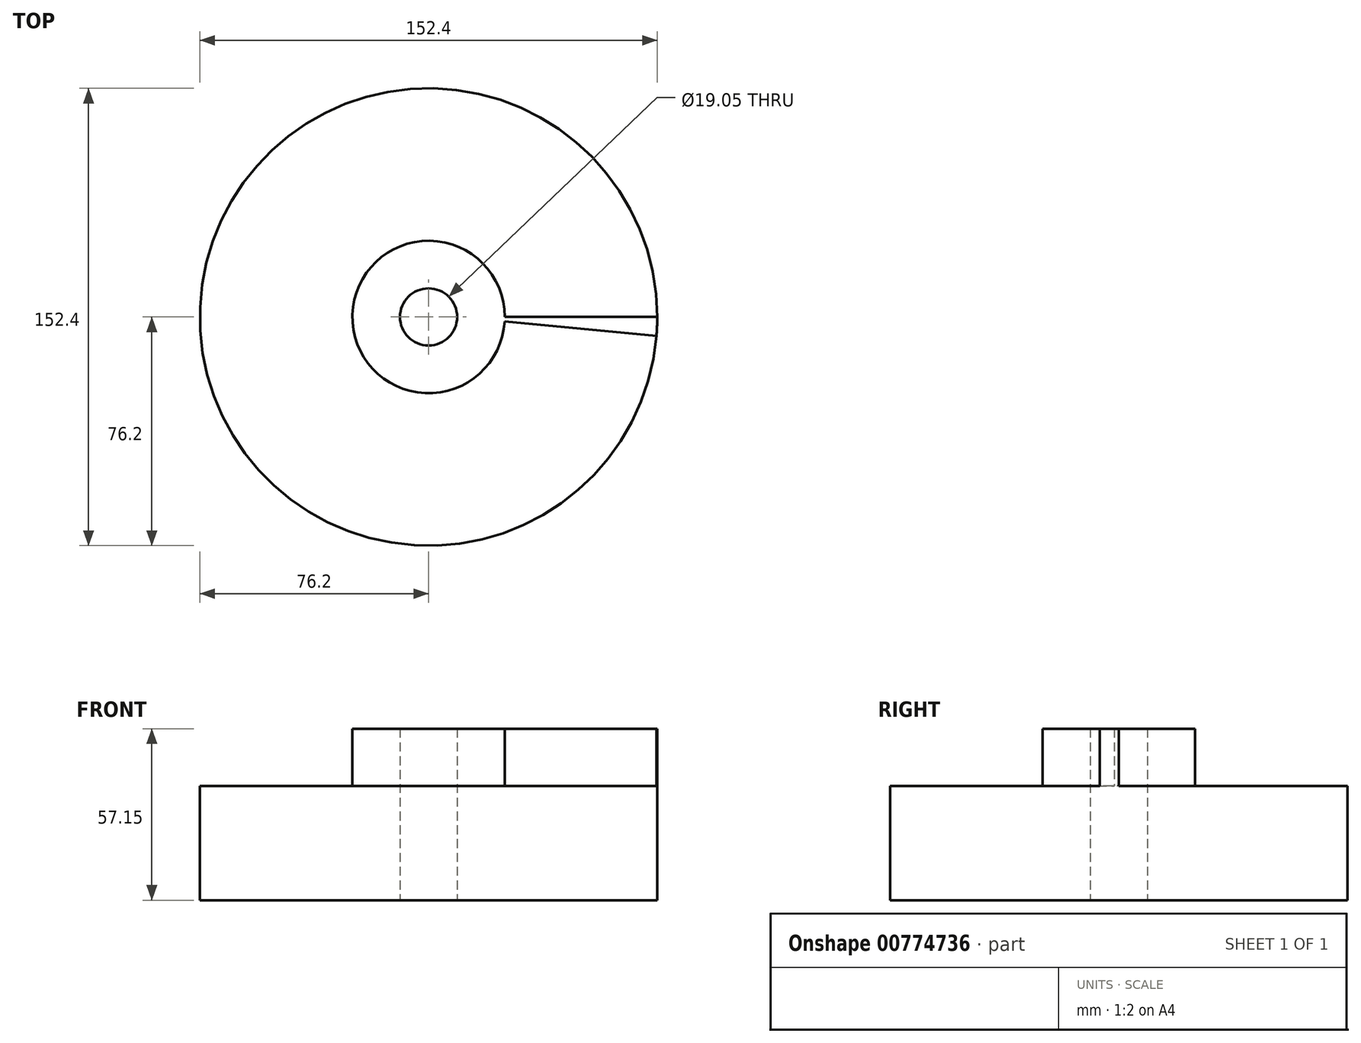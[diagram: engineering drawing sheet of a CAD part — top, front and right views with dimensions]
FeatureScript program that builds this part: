
annotation { "Feature Type Name" : "Feature", "Feature Type Description" : "" }
export const myFeature = defineFeature(function(context is Context, id is Id, definition is map)
    precondition{}
    {
        {
            var Q0;
            Q0=qCreatedBy(makeId("Top.planeOp"),FACE);
            var sketch = newSketch(context, id + "F0", { "sketchPlane" : qUnion([Q0])});
            skCircle(sketch, "E0", {"center": v(0, 0) * mm, "radius": 76.2 * mm});
            skCircle(sketch, "E1", {"center": v(0, 0) * mm, "radius": 9.53 * mm});
            skSolve(sketch);
        }
        {
            var Q0;
            Q0=makeQuery(id+"F0.imprint","IMPRINT",FACE,{"disambiguationData":[TD([[makeQuery(id+"F0.imprint","IMPRINT",EDGE,{"derivedFrom":sQuery(id+"F0.wireOp",EDGE,"E0")}),1.0]])]});
            extrude(context, id + "F1", {"entities" : qUnion([Q0]), "endBound" : BoundingType.SYMMETRIC, "depth" : 38.1 * mm, "offsetDistance" : 25.4 * mm});
        }
        {
            var Q0;
            Q0=qCreatedBy(makeId("Top.planeOp"),FACE);
            var sketch = newSketch(context, id + "F2", { "sketchPlane" : qUnion([Q0])});
            skLineSegment(sketch, "E2", {"start": v(9.52, 0) * mm, "end": v(76.2, 0) * mm});
            skLineSegment(sketch, "E3", {"start": v(75.94, -6.32) * mm, "end": v(9.52, 0) * mm});
            skArc(sketch, "E4", {"start": v(75.94, -6.32) * mm, "mid": v(76.13, -3.17) * mm, "end": v(76.2, 0) * mm});
            skPoint(sketch, "E5.orphan", {"position": v(87.84, 0) * mm});
            skSolve(sketch);
        }
        {
            var Q0;
            Q0 = qSketchRegion(id + "F2", true);
            extrude(context, id + "F3", {"entities" : qUnion([Q0]), "operationType" : NewBodyOperationType.ADD, "depth" : 38.1 * mm, "offsetDistance" : 25.4 * mm});
        }
        {
            var Q0;
            Q0=qCreatedBy(makeId("Top.planeOp"),FACE);
            var sketch = newSketch(context, id + "F4", { "sketchPlane" : qUnion([Q0])});
            skCircle(sketch, "E6", {"center": v(0, 0) * mm, "radius": 9.53 * mm});
            skCircle(sketch, "E7", {"center": v(0, 0) * mm, "radius": 25.4 * mm});
            skSolve(sketch);
        }
        {
            var Q0;
            Q0 = qSketchRegion(id + "F4", true);
            extrude(context, id + "F5", {"entities" : qUnion([Q0]), "operationType" : NewBodyOperationType.ADD, "depth" : 38.1 * mm, "offsetDistance" : 25.4 * mm});
        }
    });
